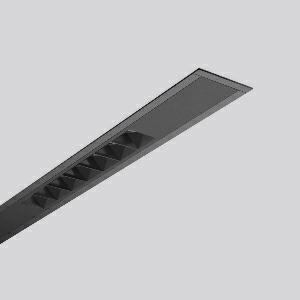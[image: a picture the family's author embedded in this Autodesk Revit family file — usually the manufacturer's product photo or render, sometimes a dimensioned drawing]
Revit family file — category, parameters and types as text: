
# Revit family: less_is_more_beamline_312472_003_1_76_f4e7
name_source: partatom
category: Lighting Fixtures
units: mm (PartAtom-declared; Revit-internal decimal feet)

## family parameters
Cut with Voids When Loaded = No
Host = Face
Light Source = No
Part Type = Normal
Room Calculation Point = No
Round Connector Dimension = Use Diameter
Shared = No

## types (1)
- LESS IS MORE BEAMLINE (1 x LED Modul 940, 1050 lm, 4000)
    Apparent Load = 35 VA
    CIE Flux Codes = 100 100 100 100 100
    Color Rendering = 92
    Color Temperature = 4000
    Default Elevation = 1800 mm
    Description = Series: LESS IS MORE BEAMLINE
Linear recessed ceiling and wall luminaire for aesthetically sophisticated lighting. Luminaire with three LED light units. Housing: extruded aluminium profile, powder-coated. End cap aluminium powder-coated. LED light unit with MRS technology: Mini-Reflector-System made of metallised thermoplastic with prismatic black glare-suppressing frame for pleasant glare-free light (RUG < 10). Each LED light unit has 7 reflector elements. Medium beam light distribution. Ceiling installation with pre-assembled SBS mounting system. LED unit with integrated converter interchangeable and removable. Suitable for through-wiring. 
Colour: deep black, matt (RAL 9005)
Length: 1702 mm
Width: 71 mm
Height: 1.5 mm
Cut-out length: 1688 mm
Cut-out width: 60 mm
Recess height: 125 mm
Luminaire: recess height: 106 mm
Lamp: LED
Socket: without socket
Colour temperature: 4000K
Colour rendering index (CRI): 90
System power: 35 W
Rated luminous flux: 3150 lm
Luminous efficiency: 90 lm/W
Control gear: Converter, dimmable, DALI
Protection class: I
Type of protection: IP 20
    Height = 0 mm  [stored 0 ft]
    Lamp = 1 x LED Modul 940
    Lamp Light Flux = 1050 lm
    Lamp count = 1
    Length = 1702 mm
    Lifetime = 50000 h
    Luminous efficacy = 90 lm/W
    Manufacturer = RZB
    ModVariant = No
    Model = 312472.003.1.76
    Mounting Place = Ceiling, Wall
    Mounting Type = Recessed
    Number of Poles = 1
    OnlyDefault = Yes
    Power Factor = 1
    Product Name = LESS IS MORE BEAMLINE
    Product group = Recessed LED linear luminaires
    ProductGroupID = 407
    Protection Class = Protection class I
    Protection Degree = IP 20
    RLX_Detail_Level = 1
    RLX_Emergency_Light_Flux = 0 lm
    RLX_Emergency_Type = 0
    RLX_Emergency_Type_DB = No
    RlxData = <blob elided: 24173 chars, md5=249e04a4>
    Socket = socket
    Standby Power = 0 W
    System Light Flux = 3150 lm
    System Power = 35 W
    Type Comments = Product without accessories
    Type Image = 312465.003.jpg
    URL = http://relux.com
    VarID = ---
    Voltage = 230 V
    Voltage Range = 220-240 V
    Weight = 0.00 kg
    Width = 71 mm

note: [stored X ft] marks values corroborated as IEEE doubles in the binary element streams (Revit-internal decimal feet)

## geometry (parser evidence)
native form markers: Blend x4, Sweep x20
no freeform markers — native parametric forms only
